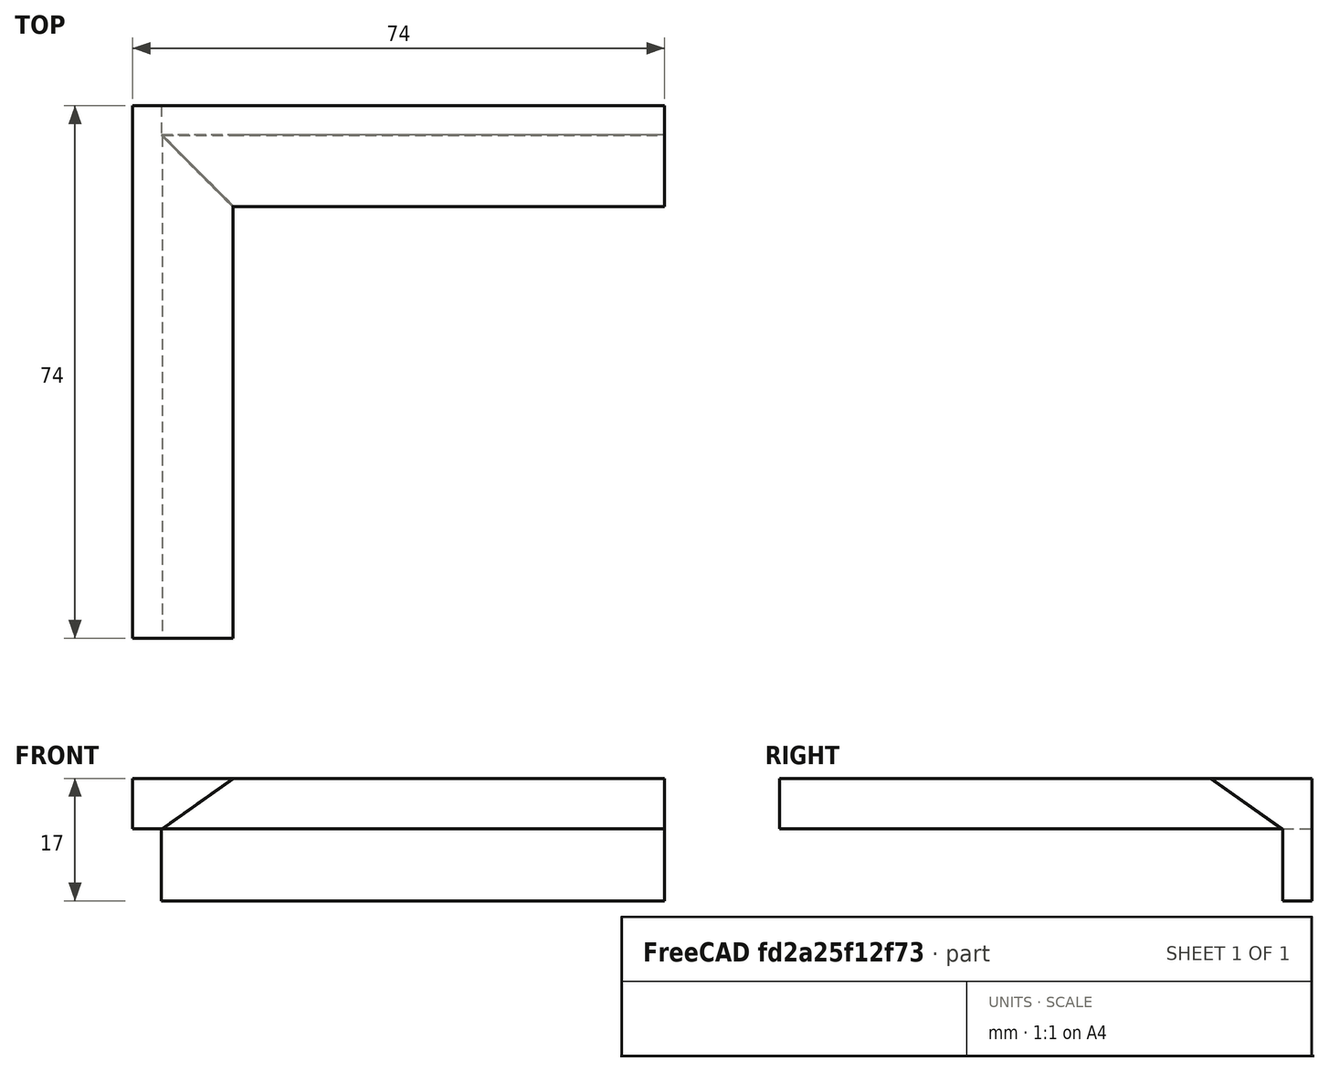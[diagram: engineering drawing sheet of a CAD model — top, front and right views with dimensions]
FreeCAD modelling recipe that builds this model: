
FCSTD DOCUMENT  (FreeCAD 0.20R29603 (Git))
Label: Entlagenschalter_Halter
License: All rights reserved
LicenseURL: http://en.wikipedia.org/wiki/All_rights_reserved
objects: PartDesign::AdditiveBox×3, PartDesign::SubtractiveWedge×2, PartDesign::Body×1
note: 11 computed .brp shape members not serialized (recipe doc carries the construction recipe); baked Part::Feature solids carry a one-line shape summary decoded from their .brp

FEATURE [PartDesign::AdditiveBox] Box001
  AttacherType = Attacher::AttachEngine3D
  Height = 7
  Length = 70
  Width = 14
FEATURE [PartDesign::AdditiveBox] Box002
  AttacherType = Attacher::AttachEngine3D
  AttachmentOffset = pos=(0,-14,0) rot=(0,0,1;0rad)
  BaseFeature = -> Box001
  Height = 10
  Length = 70
  MapMode = 5
  Placement = pos=(0,14,0) rot=(1,0,0;3.14159rad)
  Width = 4
FEATURE [PartDesign::AdditiveBox] Box003
  AttacherType = Attacher::AttachEngine3D
  AttachmentOffset = pos=(-74,-7,-10) rot=(0,0,1;0rad)
  BaseFeature = -> Box002
  Height = 14
  Length = 74
  MapMode = 5
  Placement = pos=(10,-60,7) rot=(0.57735,0.57735,-0.57735;4.18879rad)
  Support = -> [Box002]
  Width = 7
FEATURE [PartDesign::SubtractiveWedge] Wedge001
  AttacherType = Attacher::AttachEngine3D
  BaseFeature = -> Box003
  X2max = 70
  X2min = 0
  Xmax = 70
  Xmin = 9.89
  Ymax = 9.9
  Ymin = 0
  Z2max = 0
  Z2min = 0
  Zmax = 7
  Zmin = 0
FEATURE [PartDesign::SubtractiveWedge] Wedge
  AttacherType = Attacher::AttachEngine3D
  AttachmentOffset = pos=(-7,0,-70) rot=(0,0,1;0rad)
  BaseFeature = -> Wedge001
  MapMode = 5
  Placement = pos=(10,10,0) rot=(0.57735,-0.57735,0.57735;2.0944rad)
  Support = -> [Box003]
  X2max = 0
  X2min = 0
  Xmax = 7
  Xmin = 0
  Ymax = 9.89
  Ymin = 0
  Z2max = 70
  Z2min = 0
  Zmax = 70
  Zmin = 9.89
FEATURE [PartDesign::Body] Body002  label="Halter"
  Group = -> [Box001,Box002,Box003,Wedge001,Wedge]
  Origin = -> Origin002
  Tip = -> Wedge
